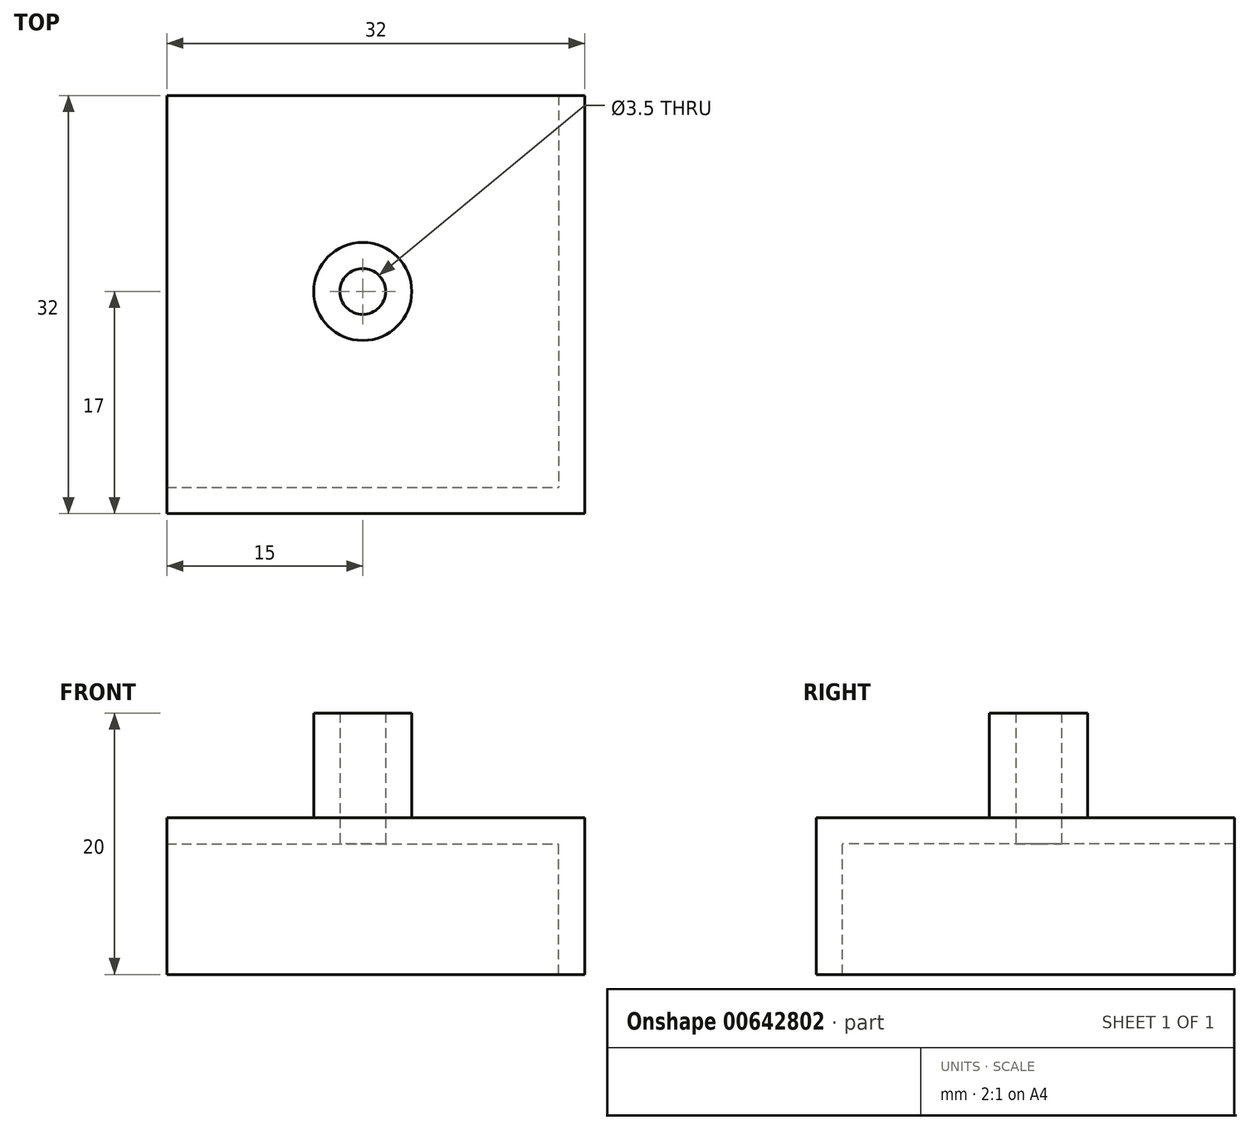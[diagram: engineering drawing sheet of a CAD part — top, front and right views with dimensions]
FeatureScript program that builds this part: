
annotation { "Feature Type Name" : "Feature", "Feature Type Description" : "" }
export const myFeature = defineFeature(function(context is Context, id is Id, definition is map)
    precondition{}
    {
        {
            var Q0;
            Q0=qCreatedBy(makeId("Top.planeOp"),FACE);
            var sketch = newSketch(context, id + "F0", { "sketchPlane" : qUnion([Q0])});
            skCircle(sketch, "E0", {"center": v(0, 0) * mm, "radius": 1.75 * mm});
            skLineSegment(sketch, "E1.bottom", {"start": v(-15, 15) * mm, "end": v(15, 15) * mm});
            skLineSegment(sketch, "E1.top", {"start": v(-15, -15) * mm, "end": v(15, -15) * mm});
            skLineSegment(sketch, "E1.left", {"start": v(-15, 15) * mm, "end": v(-15, -15) * mm});
            skLineSegment(sketch, "E1.right", {"start": v(15, 15) * mm, "end": v(15, -15) * mm});
            skLineSegment(sketch, "E2.0", {"start": v(17, 15) * mm, "end": v(17, -17) * mm});
            skLineSegment(sketch, "E2.1", {"start": v(-15, -17) * mm, "end": v(17, -17) * mm});
            skLineSegment(sketch, "E3", {"start": v(-15, -15) * mm, "end": v(-15, -17) * mm});
            skLineSegment(sketch, "E4", {"start": v(15, 15) * mm, "end": v(17, 15) * mm});
            skCircle(sketch, "E5.0", {"center": v(0, 0) * mm, "radius": 3.75 * mm});
            skSolve(sketch);
        }
        {
            var Q0;
            Q0=makeQuery(id+"F0.imprint","IMPRINT",FACE,{"disambiguationData":[TD([[makeQuery(id+"F0.imprint","IMPRINT",EDGE,{"derivedFrom":sQuery(id+"F0.wireOp",EDGE,"E0")}),-1.0]])]});
            extrude(context, id + "F1", {"entities" : qUnion([Q0]), "depth" : 10 * mm, "offsetDistance" : 25 * mm});
        }
        {
            var Q0;
            Q0=makeQuery(id+"F0.imprint","IMPRINT",FACE,{"disambiguationData":[TD([[makeQuery(id+"F0.imprint","IMPRINT",EDGE,{"derivedFrom":sQuery(id+"F0.wireOp",EDGE,"E1.bottom")}),-1.0]])]});
            var Q1;
            Q1=makeQuery(id+"F0.imprint","IMPRINT",FACE,{"disambiguationData":[TD([[makeQuery(id+"F0.imprint","IMPRINT",EDGE,{"derivedFrom":sQuery(id+"F0.wireOp",EDGE,"E1.top")}),-1.0]])]});
            extrude(context, id + "F2", {"entities" : qUnion([Q0, Q1]), "operationType" : NewBodyOperationType.ADD, "depth" : 2 * mm, "offsetDistance" : 25 * mm});
        }
        {
            var Q0;
            Q0=makeQuery(id+"F0.imprint","IMPRINT",FACE,{"disambiguationData":[TD([[makeQuery(id+"F0.imprint","IMPRINT",EDGE,{"derivedFrom":sQuery(id+"F0.wireOp",EDGE,"E1.top")}),-1.0]])]});
            extrude(context, id + "F3", {"entities" : qUnion([Q0]), "operationType" : NewBodyOperationType.ADD, "oppositeDirection" : true, "depth" : 10 * mm, "offsetDistance" : 25 * mm});
        }
    });
